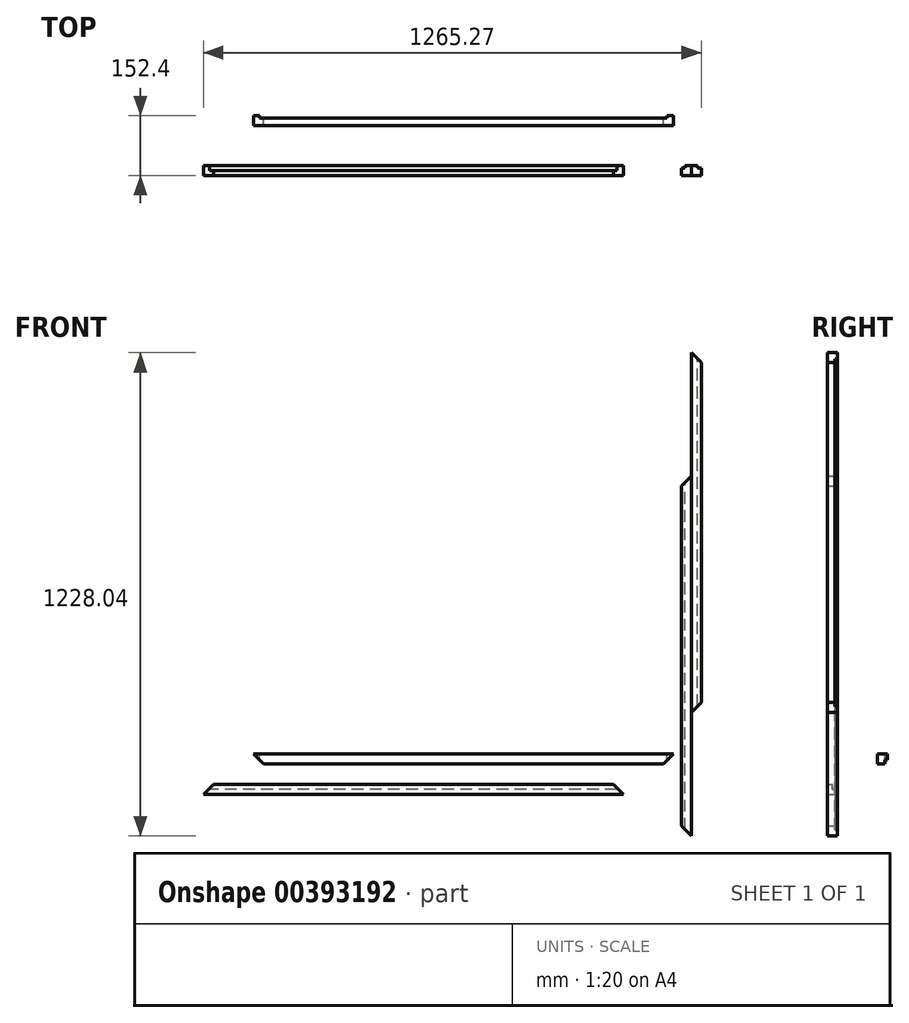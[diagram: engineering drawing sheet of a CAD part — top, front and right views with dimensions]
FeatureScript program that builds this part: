
annotation { "Feature Type Name" : "Feature", "Feature Type Description" : "" }
export const myFeature = defineFeature(function(context is Context, id is Id, definition is map)
    precondition{}
    {
        {
            var Q0;
            Q0=qCreatedBy(makeId("Front.planeOp"),FACE);
            var sketch = newSketch(context, id + "F0", { "sketchPlane" : qUnion([Q0])});
            skLineSegment(sketch, "E0.bottom", {"start": v(-547.07, 51.71) * mm, "end": v(519.73, 51.71) * mm});
            skLineSegment(sketch, "E0.top", {"start": v(-547.07, 26.31) * mm, "end": v(519.73, 26.31) * mm});
            skLineSegment(sketch, "E0.left", {"start": v(-547.07, 51.71) * mm, "end": v(-547.07, 26.31) * mm});
            skLineSegment(sketch, "E0.right", {"start": v(519.73, 51.71) * mm, "end": v(519.73, 26.31) * mm});
            skLineSegment(sketch, "E1", {"start": v(519.73, 51.71) * mm, "end": v(494.33, 26.31) * mm});
            skLineSegment(sketch, "E2", {"start": v(-13.67, 51.71) * mm, "end": v(-13.67, 26.31) * mm});
            skLineSegment(sketch, "E3.MirrorCS", {"start": v(-547.07, 51.71) * mm, "end": v(-521.67, 26.31) * mm});
            skSolve(sketch);
        }
        {
            var Q0;
            {var subQ2=sQuery(id+"F0.wireOp",EDGE,"E2");Q0=makeQuery(id+"F0.imprint","IMPRINT",FACE,{"disambiguationData":[TD([[makeQuery(id+"F0.imprint","IMPRINT",EDGE,{"derivedFrom":subQ2}),-1.0]])]});}
            var Q1;
            {var subQ0=sQuery(id+"F0.wireOp",EDGE,"E1");Q1=makeQuery(id+"F0.imprint","IMPRINT",FACE,{"disambiguationData":[TD([[makeQuery(id+"F0.imprint","IMPRINT",EDGE,{"derivedFrom":subQ0}),-1.0]])]});}
            extrude(context, id + "F1", {"entities" : qUnion([Q0, Q1]), "depth" : 25.4 * mm});
        }
        {
            var Q0;
            Q0=makeQuery(id+"F1.opExtrude","SWEPT_BODY",BODY,{"disambiguationData":[OSD([sQuery(id+"F0.wireOp",EDGE,"E0.bottom"),sQuery(id+"F0.wireOp",EDGE,"E0.top"),sQuery(id+"F0.wireOp",EDGE,"E1"),sQuery(id+"F0.wireOp",EDGE,"E3.MirrorCS")])]});
            var Q1;
            Q1=qCreatedBy(makeId("Top.planeOp"),FACE);
            mirror(context, id + "F2", {"entities" : qUnion([Q0]), "mirrorPlane" : qUnion([Q1])});
        }
        {
            var Q0;
            Q0=qCreatedBy(makeId("Front.planeOp"),FACE);
            var sketch = newSketch(context, id + "F3", { "sketchPlane" : qUnion([Q0])});
            skLineSegment(sketch, "E4.bottom", {"start": v(667.4, 757.58) * mm, "end": v(692.8, 757.58) * mm});
            skLineSegment(sketch, "E4.top", {"start": v(667.4, -156.82) * mm, "end": v(692.8, -156.82) * mm});
            skLineSegment(sketch, "E4.left", {"start": v(667.4, 757.58) * mm, "end": v(667.4, -156.82) * mm});
            skLineSegment(sketch, "E4.right", {"start": v(692.8, 757.58) * mm, "end": v(692.8, -156.82) * mm});
            skLineSegment(sketch, "E5", {"start": v(692.8, 757.58) * mm, "end": v(667.4, 732.18) * mm});
            skLineSegment(sketch, "E6", {"start": v(692.8, 300.38) * mm, "end": v(667.4, 300.38) * mm});
            skLineSegment(sketch, "E7.MirrorCS", {"start": v(692.8, -156.82) * mm, "end": v(667.4, -131.42) * mm});
            skSolve(sketch);
        }
        {
            var Q0;
            {var subQ0=sQuery(id+"F3.wireOp",EDGE,"E5");Q0=makeQuery(id+"F3.imprint","IMPRINT",FACE,{"disambiguationData":[TD([[makeQuery(id+"F3.imprint","IMPRINT",EDGE,{"derivedFrom":subQ0}),1.0]])]});}
            var Q1;
            {var subQ0=sQuery(id+"F3.wireOp",EDGE,"E6");Q1=makeQuery(id+"F3.imprint","IMPRINT",FACE,{"disambiguationData":[TD([[makeQuery(id+"F3.imprint","IMPRINT",EDGE,{"derivedFrom":subQ0}),1.0]])]});}
            extrude(context, id + "F4", {"entities" : qUnion([Q0, Q1]), "depth" : 25.4 * mm});
        }
        {
            var Q0;
            Q0=makeQuery(id+"F4.opExtrude","SWEPT_BODY",BODY,{"disambiguationData":[OSD([sQuery(id+"F3.wireOp",EDGE,"E4.left"),sQuery(id+"F3.wireOp",EDGE,"E4.right"),sQuery(id+"F3.wireOp",EDGE,"E5"),sQuery(id+"F3.wireOp",EDGE,"E7.MirrorCS")])]});
            var Q1;
            Q1=qCreatedBy(makeId("Top.planeOp"),FACE);
            mirror(context, id + "F5", {"entities" : qUnion([Q0]), "mirrorPlane" : qUnion([Q1])});
        }
        {
            var Q0;
            Q0=makeQuery(id+"F1.opExtrude","SWEPT_BODY",BODY,{"disambiguationData":[OSD([sQuery(id+"F0.wireOp",EDGE,"E0.bottom"),sQuery(id+"F0.wireOp",EDGE,"E0.top"),sQuery(id+"F0.wireOp",EDGE,"E1"),sQuery(id+"F0.wireOp",EDGE,"E3.MirrorCS")])]});
            transform(context, id + "F6", {"entities" : qUnion([Q0]), "transformType" : TransformType.TRANSLATION_3D, "dx" : 127 * mm, "dy" : 127 * mm, "dz" : 0 * mm, "makeCopy" : true});
        }
        {
            var Q0;
            Q0=makeQuery(id+"F6.opPattern","COPY",FACE,{"derivedFrom":makeQuery(id+"F1.opExtrude","SWEPT_FACE",FACE,{"disambiguationData":[OSD([sQuery(id+"F0.wireOp",EDGE,"E0.bottom")])]}),"instanceName":"1"});
            var sketch = newSketch(context, id + "F7", { "sketchPlane" : qUnion([Q0])});
            skLineSegment(sketch, "E8.bottom", {"start": v(-404.2, 127) * mm, "end": v(630.86, 127) * mm});
            skLineSegment(sketch, "E8.top", {"start": v(-404.2, 120.65) * mm, "end": v(630.86, 120.65) * mm});
            skLineSegment(sketch, "E8.left", {"start": v(-404.2, 127) * mm, "end": v(-404.2, 120.65) * mm});
            skLineSegment(sketch, "E8.right", {"start": v(630.86, 127) * mm, "end": v(630.86, 120.65) * mm});
            skSolve(sketch);
        }
        {
            var Q0;
            Q0 = qSketchRegion(id + "F7", true);
            extrude(context, id + "F8", {"entities" : qUnion([Q0]), "operationType" : NewBodyOperationType.REMOVE, "endBound" : BoundingType.THROUGH_ALL, "oppositeDirection" : true, "depth" : 25.4 * mm});
        }
        {
            var Q0;
            Q0=makeQuery(id+"F4.opExtrude","CAP_FACE",FACE,{"disambiguationData":[OSD([sQuery(id+"F3.wireOp",EDGE,"E4.left"),sQuery(id+"F3.wireOp",EDGE,"E4.right"),sQuery(id+"F3.wireOp",EDGE,"E5"),sQuery(id+"F3.wireOp",EDGE,"E7.MirrorCS")])],"isStart":true});
            var sketch = newSketch(context, id + "F9", { "sketchPlane" : qUnion([Q0])});
            skLineSegment(sketch, "E9", {"start": v(-676.93, 741.7) * mm, "end": v(-667.4, 732.18) * mm});
            skLineSegment(sketch, "E10", {"start": v(-667.4, 732.18) * mm, "end": v(-667.4, -131.42) * mm});
            skLineSegment(sketch, "E11", {"start": v(-667.4, -131.42) * mm, "end": v(-676.93, -140.95) * mm});
            skLineSegment(sketch, "E12", {"start": v(-676.93, -140.95) * mm, "end": v(-676.93, 741.7) * mm});
            skSolve(sketch);
        }
        {
            var Q0;
            Q0 = qSketchRegion(id + "F9", true);
            extrude(context, id + "F10", {"entities" : qUnion([Q0]), "operationType" : NewBodyOperationType.REMOVE, "oppositeDirection" : true, "depth" : 6.35 * mm});
        }
        {
            var Q0;
            Q0=makeQuery(id+"F5.opPattern","COPY",BODY,{"derivedFrom":makeQuery(id+"F4.opExtrude","SWEPT_BODY",BODY,{"disambiguationData":[OSD([sQuery(id+"F3.wireOp",EDGE,"E4.left"),sQuery(id+"F3.wireOp",EDGE,"E4.right"),sQuery(id+"F3.wireOp",EDGE,"E5"),sQuery(id+"F3.wireOp",EDGE,"E7.MirrorCS")])]}),"instanceName":"1"});
            var Q1;
            Q1=makeQuery(id+"F5.opPattern","COPY",EDGE,{"derivedFrom":makeQuery(id+"F4.opExtrude","SWEPT_EDGE",EDGE,{"disambiguationData":[OSD([sQuery(id+"F3.wireOp",EDGE,"E4.top"),sQuery(id+"F3.wireOp",EDGE,"E4.right"),sQuery(id+"F3.wireOp",EDGE,"E7.MirrorCS")])]}),"instanceName":"1"});
            transform(context, id + "F11", {"entities" : qUnion([Q0]), "transformType" : TransformType.ROTATION, "transformAxis" : qUnion([Q1]), "angle" : 180 * degree, "makeCopy" : false});
        }
        {
            var Q0;
            Q0=makeQuery(id+"F1.opExtrude","SWEPT_BODY",BODY,{"disambiguationData":[OSD([sQuery(id+"F0.wireOp",EDGE,"E0.bottom"),sQuery(id+"F0.wireOp",EDGE,"E0.top"),sQuery(id+"F0.wireOp",EDGE,"E1"),sQuery(id+"F0.wireOp",EDGE,"E3.MirrorCS")])]});
            deleteBodies(context, id + "F12", {"entities" : qUnion([Q0])});
        }
        {
            var Q0;
            Q0=makeQuery(id+"F5.opPattern","COPY",BODY,{"derivedFrom":makeQuery(id+"F4.opExtrude","SWEPT_BODY",BODY,{"disambiguationData":[OSD([sQuery(id+"F3.wireOp",EDGE,"E4.left"),sQuery(id+"F3.wireOp",EDGE,"E4.right"),sQuery(id+"F3.wireOp",EDGE,"E5"),sQuery(id+"F3.wireOp",EDGE,"E7.MirrorCS")])]}),"instanceName":"1"});
            deleteBodies(context, id + "F13", {"entities" : qUnion([Q0])});
        }
        {
            var Q0;
            Q0=makeQuery(id+"F4.opExtrude","SWEPT_BODY",BODY,{"disambiguationData":[OSD([sQuery(id+"F3.wireOp",EDGE,"E4.left"),sQuery(id+"F3.wireOp",EDGE,"E4.right"),sQuery(id+"F3.wireOp",EDGE,"E5"),sQuery(id+"F3.wireOp",EDGE,"E7.MirrorCS")])]});
            var Q1;
            Q1=qCreatedBy(makeId("Top.planeOp"),FACE);
            mirror(context, id + "F14", {"entities" : qUnion([Q0]), "mirrorPlane" : qUnion([Q1])});
        }
        {
            var Q0;
            Q0=makeQuery(id+"F14.opPattern","COPY",BODY,{"derivedFrom":makeQuery(id+"F4.opExtrude","SWEPT_BODY",BODY,{"disambiguationData":[OSD([sQuery(id+"F3.wireOp",EDGE,"E4.left"),sQuery(id+"F3.wireOp",EDGE,"E4.right"),sQuery(id+"F3.wireOp",EDGE,"E5"),sQuery(id+"F3.wireOp",EDGE,"E7.MirrorCS")])]}),"instanceName":"1"});
            var Q1;
            Q1=makeQuery(id+"F14.opPattern","COPY",EDGE,{"derivedFrom":makeQuery(id+"F4.opExtrude","SWEPT_EDGE",EDGE,{"disambiguationData":[OSD([sQuery(id+"F3.wireOp",EDGE,"E4.top"),sQuery(id+"F3.wireOp",EDGE,"E4.right"),sQuery(id+"F3.wireOp",EDGE,"E7.MirrorCS")])]}),"instanceName":"1"});
            transform(context, id + "F15", {"entities" : qUnion([Q0]), "transformType" : TransformType.ROTATION, "transformAxis" : qUnion([Q1]), "angle" : 180 * degree, "makeCopy" : false});
        }
        {
            var Q0;
            Q0=makeQuery(id+"F2.opPattern","COPY",FACE,{"derivedFrom":makeQuery(id+"F1.opExtrude","SWEPT_FACE",FACE,{"disambiguationData":[OSD([sQuery(id+"F0.wireOp",EDGE,"E0.top")])]}),"instanceName":"1"});
            var sketch = newSketch(context, id + "F16", { "sketchPlane" : qUnion([Q0])});
            skPoint(sketch, "E13.firstSnap0", {"position": v(494.33, -12.7) * mm});
            skLineSegment(sketch, "E13.bottom", {"start": v(503.86, -12.7) * mm, "end": v(-531.2, -12.7) * mm});
            skLineSegment(sketch, "E13.top", {"start": v(503.86, 0) * mm, "end": v(-531.2, 0) * mm});
            skLineSegment(sketch, "E13.left", {"start": v(503.86, -12.7) * mm, "end": v(503.86, 0) * mm});
            skLineSegment(sketch, "E13.right", {"start": v(-531.2, -12.7) * mm, "end": v(-531.2, 0) * mm});
            skSolve(sketch);
        }
        {
            var Q0;
            Q0 = qSketchRegion(id + "F16", true);
            extrude(context, id + "F17", {"entities" : qUnion([Q0]), "operationType" : NewBodyOperationType.REMOVE, "oppositeDirection" : true, "depth" : 12.7 * mm});
        }
    });
